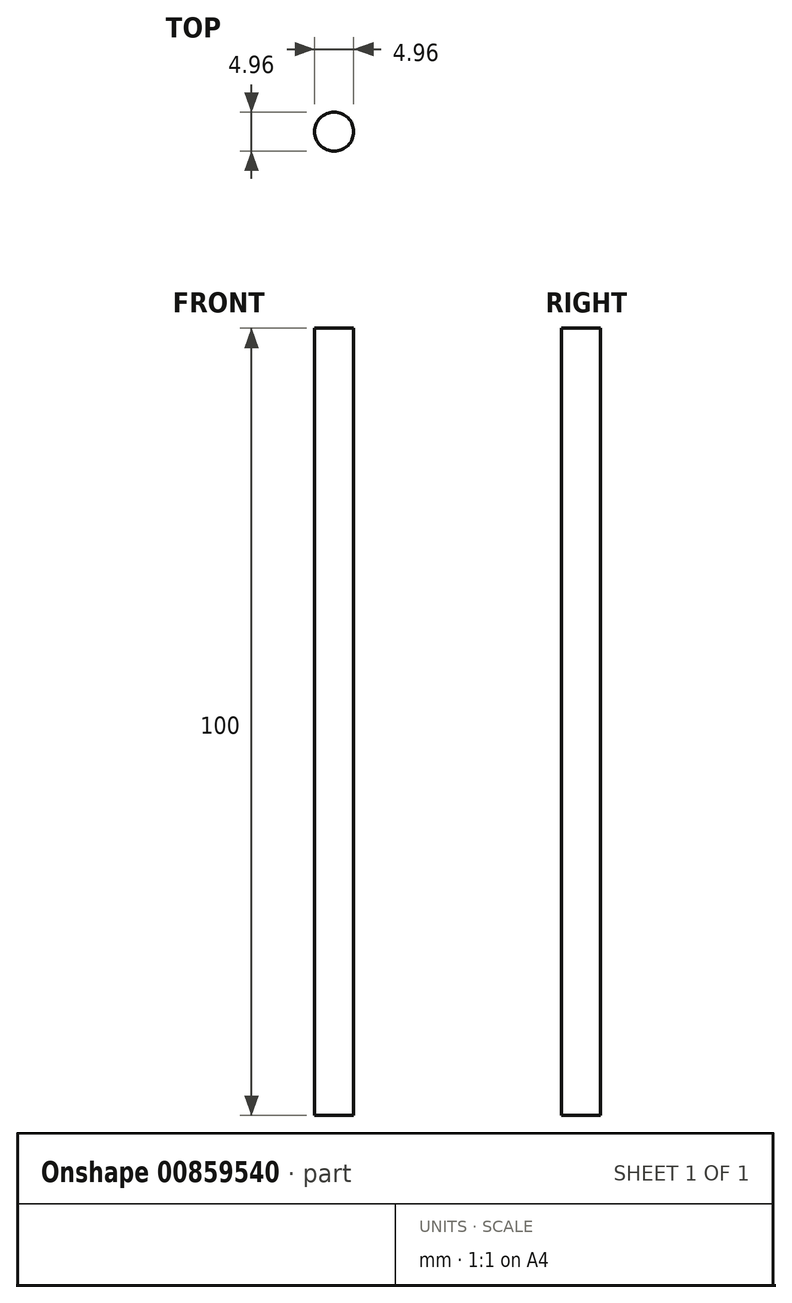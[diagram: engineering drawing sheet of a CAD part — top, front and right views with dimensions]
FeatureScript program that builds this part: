
annotation { "Feature Type Name" : "Feature", "Feature Type Description" : "" }
export const myFeature = defineFeature(function(context is Context, id is Id, definition is map)
    precondition{}
    {
        {
            var Q0;
            Q0=qCreatedBy(makeId("Top.planeOp"),FACE);
            var sketch = newSketch(context, id + "F0", { "sketchPlane" : qUnion([Q0])});
            skCircle(sketch, "E0", {"center": v(0, 0) * mm, "radius": 2.48 * mm});
            skSolve(sketch);
        }
        {
            var Q0;
            Q0=makeQuery(id+"F0.imprint","IMPRINT",FACE,{"disambiguationData":[TD([[makeQuery(id+"F0.imprint","IMPRINT",EDGE,{"derivedFrom":sQuery(id+"F0.wireOp",EDGE,"E0")}),1.0]])]});
            extrude(context, id + "F1", {"entities" : qUnion([Q0]), "depth" : 100 * mm, "offsetDistance" : 25 * mm});
        }
    });
